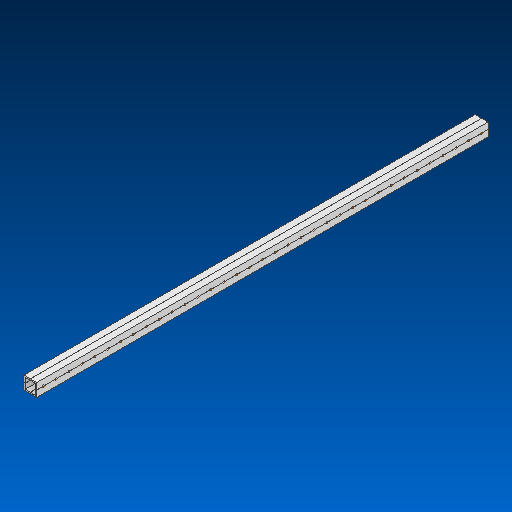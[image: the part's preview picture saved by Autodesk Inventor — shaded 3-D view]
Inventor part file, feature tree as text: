
AUTODESK INVENTOR PART (.ipt)
format: ipt  version: 2022.2 (Build 262287000, 287)  size: 797,696 bytes
history: native  units: in
note: dims shown in document units (in); Inventor stores cm internally (conversion verified against a paired STEP export)
features: other x35, extrude x1, pattern_linear x1, sketch x1, pattern_circular x1
ambient origin geometry x8: Origin, YZ Plane, XZ Plane, XY Plane, X Axis, Y Axis, Z Axis, Center Point
bodies: Solid1 (feature_tree)
feature tree (39):
  extrude  "Extrusion1"  Depth=1.0in
  other  "Work Axis1"
  pattern_linear  "Rectangular Pattern1"  Spacing1=0.0in  [1 undecoded]
  sketch  "Sketch1"  dims[d0=1.0in d1=24.0in d2=0.0in d3=13.7795in d5=1.0in]
  other  "Work Axis2"
  other  "Work Axis3"
  other  "Work Axis4"
  other  "Work Axis5"
  other  "Work Axis6"
  other  "Work Axis7"
  other  "Work Axis8"
  other  "Work Axis9"
  other  "Work Axis10"
  other  "Work Axis11"
  other  "Work Axis12"
  other  "Work Axis13"
  other  "Work Axis14"
  other  "Work Axis15"
  other  "Work Axis16"
  other  "Work Axis17"
  other  "Work Axis18"
  other  "Work Axis19"
  other  "Work Axis20"
  other  "Work Axis21"
  other  "Work Axis22"
  other  "Work Axis23"
  other  "Work Axis24"
  other  "Work Axis25"
  other  "Work Axis26"
  other  "Work Axis27"
  other  "Work Axis28"
  other  "Work Axis29"
  other  "Work Axis30"
  other  "Work Axis31"
  other  "Work Axis32"
  other  "Work Axis33"
  other  "Work Axis34"
  other  "Work Axis35"
  pattern_circular  "CirPattern2"
note: 1 required parameter value undecoded (feature->parameter linkage not recoverable at this tier; creation-order binding heuristic only, values carry confidence <= 0.55)
